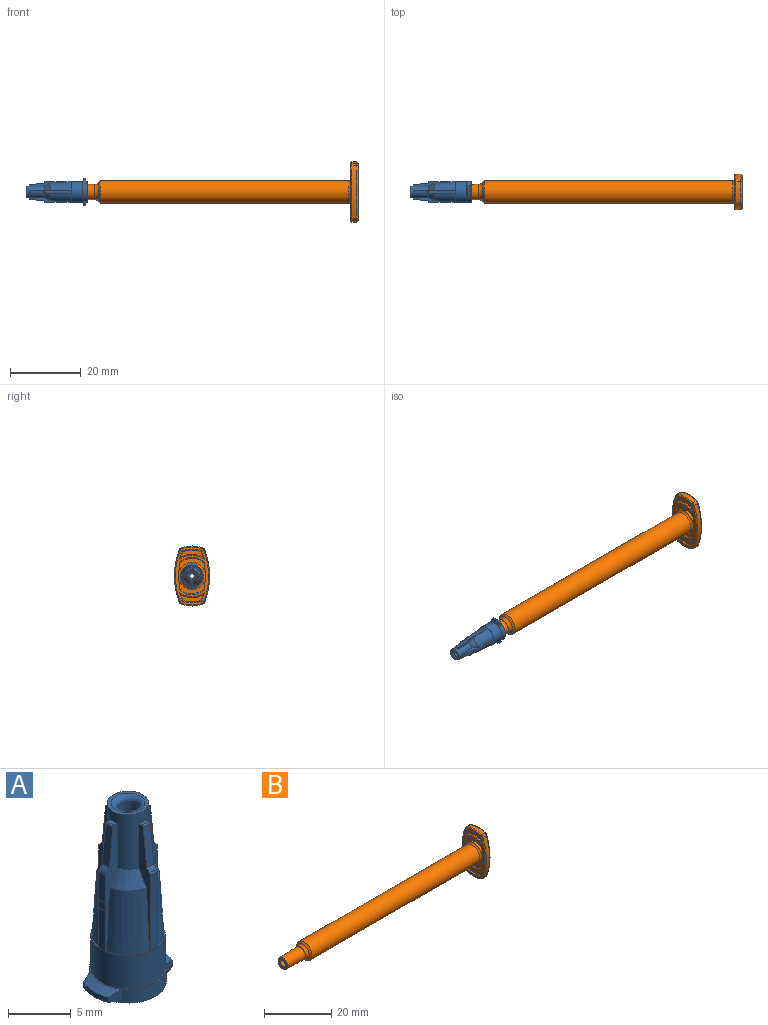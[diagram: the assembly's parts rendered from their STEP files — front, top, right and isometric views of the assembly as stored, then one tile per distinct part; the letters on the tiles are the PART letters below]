
ASSEMBLY  parts=2 mates=1
PART A: 78 faces, bbox 7.9x6.2x17.4 mm
  f0: plane 5.9x5.9mm, normal (0,0,1), area 1.6mm2, adj f1,f3,f5,f14,f15,f44,f46,f47
  f1: cone r=2.5mm half-angle=3.3deg, axis (0,0,-1), area 20.4mm2, adj f0,f2,f47,f77
  f2: cone r=1.65mm half-angle=29.5deg, axis (0,0,-1), area 4.2mm2, adj f1,f17,f47,f77
  f3: cone r=2.5mm half-angle=3.3deg, axis (0,0,-1), area 20.4mm2, adj f0,f4,f46,f67
  f4: cone r=1.65mm half-angle=29.5deg, axis (0,0,-1), area 4.2mm2, adj f3,f17,f46,f67
  f5: cone r=2.5mm half-angle=3.3deg, axis (0,0,-1), area 20.4mm2, adj f0,f6,f57,f76
  f6: cone r=1.65mm half-angle=29.5deg, axis (0,0,-1), area 4.2mm2, adj f5,f17,f57,f76
  f7: cylinder r=3.89mm len=2.81mm, axis (0,0,1), area 1.4mm2, adj f10,f12,f35,f37
  f8: cylinder r=3.89mm len=2.81mm, axis (0,0,1), area 1.4mm2, adj f9,f11,f34,f36
  f9: cone r=3.05mm half-angle=75deg, axis (0,0,1), area 2.9mm2, adj f8,f33,f34,f36
  f10: cone r=3.05mm half-angle=75deg, axis (0,0,1), area 2.9mm2, adj f7,f33,f35,f37
  f11: cone r=3.89mm half-angle=65deg, axis (0,0,-1), area 3.1mm2, adj f8,f13,f34,f36
  f12: cone r=3.89mm half-angle=65deg, axis (0,0,-1), area 3.1mm2, adj f7,f13,f35,f37
  f13: cone r=2.95mm half-angle=89.9deg, axis (0,0,-1), area 1.9mm2, adj f11,f12,f14,f33
  f14: cylinder r=2.95mm len=5.9mm, axis (0,0,1), area 59.3mm2, adj f0,f13
  f15: cone r=2.5mm half-angle=3.3deg, axis (0,0,-1), area 20.4mm2, adj f0,f16,f56,f66
  f16: cone r=1.65mm half-angle=29.5deg, axis (0,0,-1), area 4.2mm2, adj f15,f17,f56,f66
  f17: cylinder r=1.65mm len=5.3mm, axis (0,0,1), area 41mm2, adj f2,f4,f6,f16,f18,f43,f46,f47
  f18: plane 3.3x3.3mm, normal (0,0,1), area 2.8mm2, adj f17,f19
  f19: torus R=1.35mm, axis (0,0,1), area 5.1mm2, adj f18,f20
  f20: cylinder r=0.85mm len=5.8mm, axis (0,0,1), area 31mm2, adj f19,f21
  f21: plane 1.7x1.7mm, normal (0,0,1), area 0.6mm2, adj f20,f22
  f22: cylinder r=0.72mm len=1.45mm, axis (0,0,1), area 3.6mm2, adj f21,f23
  f23: plane 2.7x2.7mm, normal (0,0,-1), area 4.1mm2, adj f22,f24
  f24: cylinder r=1.35mm len=2.7mm, axis (0,0,1), area 2.5mm2, adj f23,f25
  f25: torus R=1.32mm, axis (0,0,1), area 7.5mm2, adj f24,f26
  f26: cone r=1.84mm half-angle=1.7deg, axis (0,0,-1), area 7.2mm2, adj f25,f27
  f27: torus R=1.54mm, axis (0,0,1), area 2.6mm2, adj f26,f28
  f28: torus R=2.24mm, axis (0,0,1), area 9.9mm2, adj f27,f29
  f29: torus R=1.58mm, axis (0,0,1), area 2.6mm2, adj f28,f30
  f30: cone r=1.88mm half-angle=1.7deg, axis (0,0,-1), area 99mm2, adj f29,f31
  f31: torus R=2.36mm, axis (0,0,1), area 5.3mm2, adj f30,f32
  f32: plane 6.1x6.1mm, normal (0,0,-1), area 11.7mm2, adj f31,f33
  f33: cylinder r=3.05mm len=6.1mm, axis (0,0,1), area 16.7mm2, adj f9,f10,f13,f32,f34,f35,f36,f37
  f34: plane 1.25x1.22mm, normal (-0.29,0.96,0), area 0.9mm2, adj f8,f9,f11,f33
  f35: plane 1.25x1.22mm, normal (0.29,0.96,0), area 0.9mm2, adj f7,f10,f12,f33
  f36: plane 1.25x1.22mm, normal (-0.29,-0.96,0), area 0.9mm2, adj f8,f9,f11,f33
  f37: plane 1.25x1.22mm, normal (0.29,-0.96,0), area 0.9mm2, adj f7,f10,f12,f33
  f38: plane 2.7x0.8mm, normal (0,1,-0.01), area 2.2mm2, adj f39,f45,f46,f47
  f39: cylinder r=0.3mm len=0.8mm, axis (-1,0,0), area 0.2mm2, adj f38,f40,f46,f47
  f40: plane 0.8x0.32mm, normal (0,0.71,0.71), area 0.4mm2, adj f39,f41,f46,f47
  f41: plane 3.76x0.8mm, normal (0,0.99,0.1), area 3mm2, adj f40,f42,f46,f47
  f42: cylinder r=0.15mm len=0.8mm, axis (-1,0,0), area 0.2mm2, adj f41,f43,f46,f47
  f43: plane 0.8x0.36mm, normal (0,0,1), area 0.3mm2, adj f17,f42,f46,f47
  f44: plane 3.9x0.8mm, normal (0,1,0.01), area 3.1mm2, adj f0,f45,f46,f47
  f45: plane 0.8x0.77mm, normal (0,1,0), area 0.6mm2, adj f38,f44,f46,f47
  f46: plane 11.84x1.35mm, normal (1,0,0), area 5.9mm2, adj f0,f3,f4,f17,f38,f39,f40,f41
  f47: plane 11.84x1.35mm, normal (-1,0,0), area 5.9mm2, adj f0,f1,f2,f17,f38,f39,f40,f41
  f48: plane 0.8x0.36mm, normal (0,0,1), area 0.3mm2, adj f17,f49,f56,f57
  f49: cylinder r=0.15mm len=0.8mm, axis (-1,0,0), area 0.2mm2, adj f48,f50,f56,f57
  f50: plane 3.76x0.8mm, normal (0,-0.99,0.1), area 3mm2, adj f49,f51,f56,f57
  f51: plane 0.8x0.32mm, normal (0,-0.71,0.71), area 0.4mm2, adj f50,f52,f56,f57
  f52: cylinder r=0.3mm len=0.8mm, axis (-1,0,0), area 0.2mm2, adj f51,f53,f56,f57
  f53: plane 2.7x0.8mm, normal (0,-1,-0.01), area 2.2mm2, adj f52,f54,f56,f57
  f54: plane 0.8x0.77mm, normal (0,-1,0), area 0.6mm2, adj f53,f55,f56,f57
  f55: plane 3.9x0.8mm, normal (0,-1,0.01), area 3.1mm2, adj f0,f54,f56,f57
  f56: plane 11.84x1.35mm, normal (1,0,0), area 5.9mm2, adj f0,f15,f16,f17,f48,f49,f50,f51
  f57: plane 11.84x1.35mm, normal (-1,0,0), area 5.9mm2, adj f0,f5,f6,f17,f48,f49,f50,f51
  f58: plane 2.7x0.8mm, normal (1,0,-0.01), area 2.2mm2, adj f59,f65,f66,f67
  f59: cylinder r=0.3mm len=0.8mm, axis (0,1,0), area 0.2mm2, adj f58,f60,f66,f67
  f60: plane 0.8x0.32mm, normal (0.71,0,0.71), area 0.4mm2, adj f59,f61,f66,f67
  f61: plane 3.76x0.8mm, normal (0.99,0,0.1), area 3mm2, adj f60,f62,f66,f67
  f62: cylinder r=0.15mm len=0.8mm, axis (0,1,0), area 0.2mm2, adj f61,f63,f66,f67
  f63: plane 0.8x0.36mm, normal (0,0,1), area 0.3mm2, adj f17,f62,f66,f67
  f64: plane 3.9x0.8mm, normal (1,0,0.01), area 3.1mm2, adj f0,f65,f66,f67
  f65: plane 0.8x0.77mm, normal (1,0,0), area 0.6mm2, adj f58,f64,f66,f67
  f66: plane 11.84x1.35mm, normal (0,-1,0), area 5.9mm2, adj f0,f15,f16,f17,f58,f59,f60,f61
  f67: plane 11.84x1.35mm, normal (0,1,0), area 5.9mm2, adj f0,f3,f4,f17,f58,f59,f60,f61
  f68: plane 0.8x0.36mm, normal (0,0,1), area 0.3mm2, adj f17,f69,f76,f77
  f69: cylinder r=0.15mm len=0.8mm, axis (0,1,0), area 0.2mm2, adj f68,f70,f76,f77
  f70: plane 3.76x0.8mm, normal (-0.99,0,0.1), area 3mm2, adj f69,f71,f76,f77
  f71: plane 0.8x0.32mm, normal (-0.71,0,0.71), area 0.4mm2, adj f70,f72,f76,f77
  f72: cylinder r=0.3mm len=0.8mm, axis (0,1,0), area 0.2mm2, adj f71,f73,f76,f77
  f73: plane 2.7x0.8mm, normal (-1,0,-0.01), area 2.2mm2, adj f72,f74,f76,f77
  f74: plane 0.8x0.77mm, normal (-1,0,0), area 0.6mm2, adj f73,f75,f76,f77
  f75: plane 3.9x0.8mm, normal (-1,0,0.01), area 3.1mm2, adj f0,f74,f76,f77
  f76: plane 11.84x1.35mm, normal (0,-1,0), area 5.9mm2, adj f0,f5,f6,f17,f68,f69,f70,f71
  f77: plane 11.84x1.35mm, normal (0,1,0), area 5.9mm2, adj f0,f1,f2,f17,f68,f69,f70,f71
PART B: 74 faces, bbox 82.3x11x17.4 mm
  f0: plane 16.41x9.41mm, normal (-1,0,0), area 38.2mm2, adj f3,f34,f36,f39,f41,f48,f49,f50
  f1: cylinder r=8.5mm len=6.03mm, axis (1,0,0), area 8.6mm2, adj f25,f27,f49,f58
  f2: cylinder r=8.5mm len=6.03mm, axis (1,0,0), area 8.6mm2, adj f24,f26,f54,f61
  f3: torus R=3.8mm, axis (1,0,0), area 20.2mm2, adj f0,f4,f35,f38
  f4: cylinder r=3.2mm len=70.4mm, axis (1,0,0), area 1415.5mm2, adj f3,f5
  f5: cone r=3.2mm half-angle=46.7deg, axis (1,0,0), area 13.7mm2, adj f4,f6
  f6: torus R=3.69mm, axis (1,0,0), area 18mm2, adj f5,f7
  f7: cone r=2.19mm half-angle=0deg, axis (1,0,0), area 1.4mm2, adj f6,f8
  f8: cone r=1.97mm half-angle=1.7deg, axis (1,0,0), area 94.8mm2, adj f7,f9
  f9: torus R=1.72mm, axis (1,0,0), area 4.5mm2, adj f8,f10
  f10: plane 3.44x3.44mm, normal (-1,0,0), area 3.5mm2, adj f9,f11
  f11: cone r=1.35mm half-angle=15deg, axis (-1,0,0), area 1.7mm2, adj f10,f12
  f12: plane 2.6x2.6mm, normal (-1,0,0), area 1.8mm2, adj f11,f13
  f13: cone r=1.29mm half-angle=1.6deg, axis (1,0,0), area 62mm2, adj f12,f14
  f14: torus R=2.29mm, axis (1,0,0), area 6.9mm2, adj f13,f15
  f15: cone r=1.6mm half-angle=46.7deg, axis (1,0,0), area 12.9mm2, adj f14,f16
  f16: cylinder r=2.35mm len=67.56mm, axis (1,0,0), area 999.6mm2, adj f15,f17
  f17: cone r=2.36mm half-angle=0.8deg, axis (1,0,0), area 5.2mm2, adj f16,f18
  f18: cylinder r=2.36mm len=4.72mm, axis (1,0,0), area 19.3mm2, adj f17,f19
  f19: cone r=2.36mm half-angle=18.9deg, axis (-1,0,0), area 5.3mm2, adj f18,f20
  f20: cone r=2.93mm half-angle=14.8deg, axis (1,0,0), area 43.6mm2, adj f19,f21
  f21: plane 16.41x9.41mm, normal (1,0,0), area 105.7mm2, adj f20,f56,f57,f58,f59,f60,f61,f62
  f22: cylinder r=20mm len=14.76mm, axis (1,0,0), area 21.2mm2, adj f24,f25,f53,f62
  f23: cylinder r=20mm len=14.76mm, axis (1,0,0), area 21.2mm2, adj f26,f27,f50,f57
  f24: bspline ~2.2x0.58mm, area 1.2mm2, adj f2,f22,f55,f63
  f25: bspline ~2.2x0.58mm, area 1.2mm2, adj f1,f22,f51,f60
  f26: bspline ~2.2x0.58mm, area 1.2mm2, adj f2,f23,f52,f59
  f27: bspline ~2.2x0.58mm, area 1.2mm2, adj f1,f23,f48,f56
  f28: cylinder r=6.14mm len=6.12mm, axis (-1,0,0), area 1.9mm2, adj f29,f31,f32,f67
  f29: cylinder r=20mm len=1.56mm, axis (-1,0,0), area 0.5mm2, adj f28,f30,f32,f66
  f30: cylinder r=7.34mm len=5.12mm, axis (-1,0,0), area 1.6mm2, adj f29,f31,f32,f68
  f31: cylinder r=20mm len=1.56mm, axis (-1,0,0), area 0.5mm2, adj f28,f30,f32,f69
  f32: plane 6.12x2.02mm, normal (-1,0,0), area 7mm2, adj f28,f29,f30,f31
  f33: cylinder r=4.98mm len=6.91mm, axis (-1,0,0), area 2.3mm2, adj f34,f36,f37,f65
  f34: cylinder r=20mm len=3.64mm, axis (-1,0,0), area 2mm2, adj f0,f33,f35,f37,f65
  f35: cylinder r=3.8mm len=7.55mm, axis (-1,0,0), area 6.6mm2, adj f3,f34,f36,f37
  f36: cylinder r=20mm len=3.64mm, axis (-1,0,0), area 2mm2, adj f0,f33,f35,f37,f65
  f37: plane 7.55x4.55mm, normal (-1,0,0), area 10.3mm2, adj f33,f34,f35,f36
  f38: cylinder r=3.8mm len=7.55mm, axis (-1,0,0), area 6.6mm2, adj f3,f39,f41,f42
  f39: cylinder r=20mm len=3.64mm, axis (-1,0,0), area 2mm2, adj f0,f38,f40,f42,f64
  f40: cylinder r=4.98mm len=6.91mm, axis (-1,0,0), area 2.3mm2, adj f39,f41,f42,f64
  f41: cylinder r=20mm len=3.64mm, axis (-1,0,0), area 2mm2, adj f0,f38,f40,f42,f64
  f42: plane 7.55x4.55mm, normal (-1,0,0), area 10.3mm2, adj f38,f39,f40,f41
  f43: cylinder r=7.34mm len=5.12mm, axis (-1,0,0), area 1.6mm2, adj f44,f46,f47,f71
  f44: cylinder r=20mm len=1.56mm, axis (-1,0,0), area 0.5mm2, adj f43,f45,f47,f70
  f45: cylinder r=6.14mm len=6.12mm, axis (-1,0,0), area 1.9mm2, adj f44,f46,f47,f72
  f46: cylinder r=20mm len=1.56mm, axis (-1,0,0), area 0.5mm2, adj f43,f45,f47,f73
  f47: plane 6.12x2.02mm, normal (-1,0,0), area 7mm2, adj f43,f44,f45,f46
  f48: bspline ~0.68x0.68mm, area 0.4mm2, adj f0,f27,f49,f50
  f49: bspline ~6.03x1.02mm, area 3mm2, adj f0,f1,f48,f51
  f50: bspline ~14.76x2.17mm, area 7.3mm2, adj f0,f23,f48,f52
  f51: bspline ~0.68x0.68mm, area 0.4mm2, adj f0,f25,f49,f53
  f52: bspline ~0.68x0.68mm, area 0.4mm2, adj f0,f26,f50,f54
  f53: bspline ~14.76x2.17mm, area 7.3mm2, adj f0,f22,f51,f55
  f54: bspline ~6.03x1.02mm, area 3mm2, adj f0,f2,f52,f55
  f55: bspline ~0.68x0.68mm, area 0.4mm2, adj f0,f24,f53,f54
  f56: bspline ~0.68x0.68mm, area 0.4mm2, adj f21,f27,f57,f58
  f57: bspline ~14.76x2.17mm, area 7.3mm2, adj f21,f23,f56,f59
  f58: bspline ~6.03x1.02mm, area 3mm2, adj f1,f21,f56,f60
  f59: bspline ~0.68x0.68mm, area 0.4mm2, adj f21,f26,f57,f61
  f60: bspline ~0.68x0.68mm, area 0.4mm2, adj f21,f25,f58,f62
  f61: bspline ~6.03x1.02mm, area 3mm2, adj f2,f21,f59,f63
  f62: bspline ~14.76x2.17mm, area 7.3mm2, adj f21,f22,f60,f63
  f63: bspline ~0.68x0.68mm, area 0.4mm2, adj f21,f24,f61,f62
  f64: bspline ~7.89x2.13mm, area 3.6mm2, adj f0,f39,f40,f41
  f65: bspline ~7.89x2.13mm, area 3.6mm2, adj f0,f33,f34,f36
  f66: bspline ~2.73x1.09mm, area 1mm2, adj f0,f29,f67,f68
  f67: bspline ~7.45x1.5mm, area 3.5mm2, adj f0,f28,f66,f69
  f68: bspline ~5.59x0.81mm, area 2.7mm2, adj f0,f30,f66,f69
  f69: bspline ~2.73x1.09mm, area 1mm2, adj f0,f31,f67,f68
  f70: bspline ~2.73x1.09mm, area 1mm2, adj f0,f44,f71,f72
  f71: bspline ~5.59x0.81mm, area 2.7mm2, adj f0,f43,f70,f73
  f72: bspline ~7.45x1.5mm, area 3.5mm2, adj f0,f45,f70,f73
  f73: bspline ~2.73x1.09mm, area 1mm2, adj f0,f46,f71,f72
PLACE A rot(axis=(0.71,0,-0.71),180deg) t=(475.9,0,-19.96)mm
PLACE B t=(552.6,0,-19.96)mm
MATE slider A.f1 <-> B.f11  axis (1,0,0) through (475.9,0,-19.96)mm
